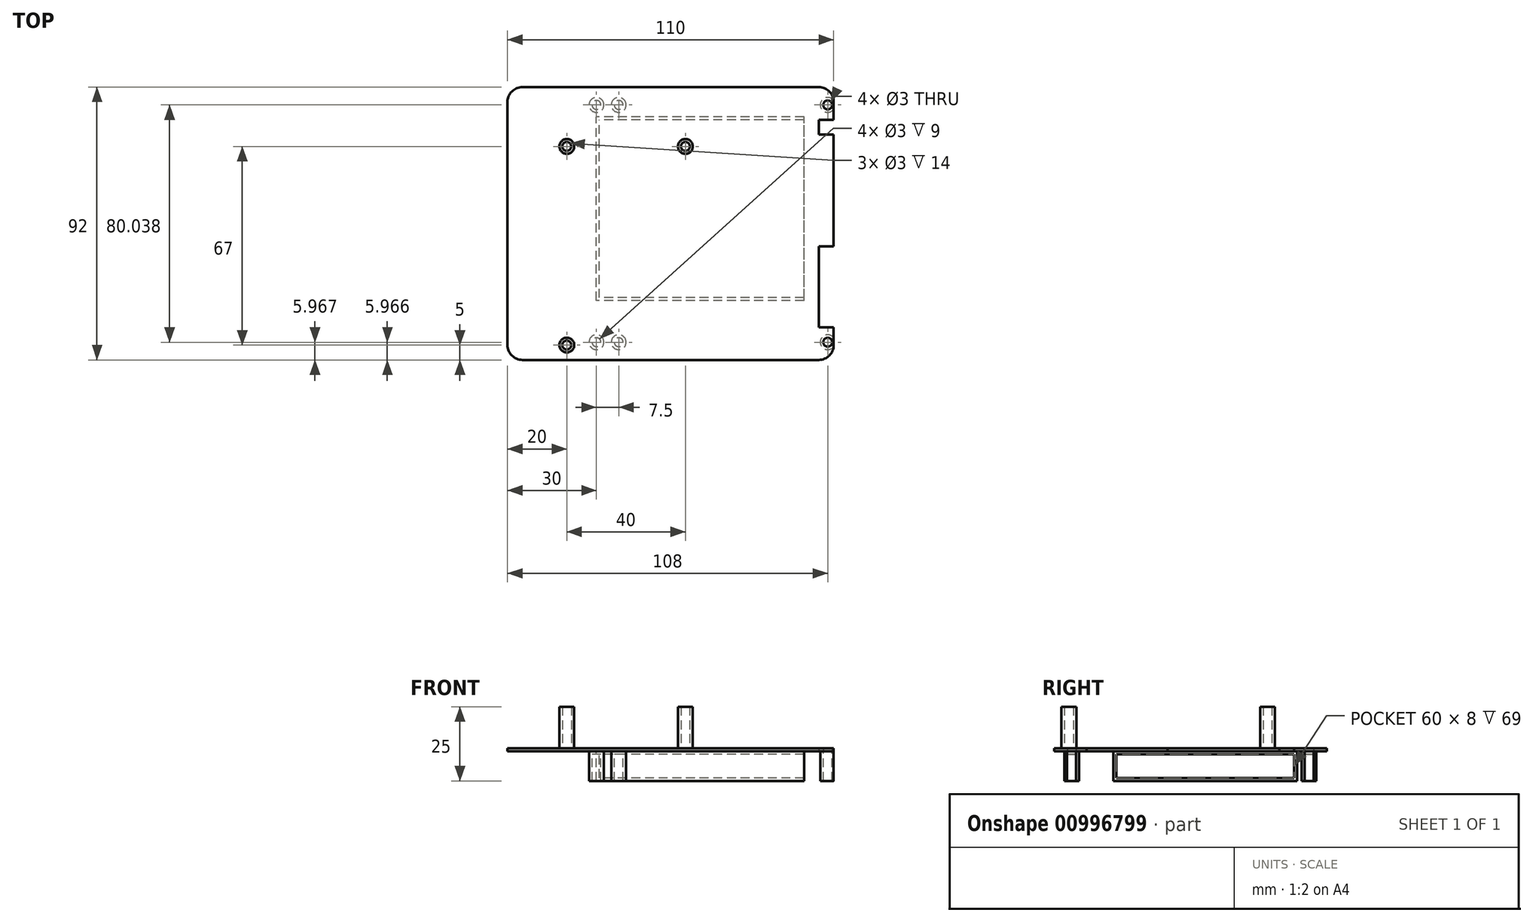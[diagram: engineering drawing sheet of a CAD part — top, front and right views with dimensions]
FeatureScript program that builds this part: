
annotation { "Feature Type Name" : "Feature", "Feature Type Description" : "" }
export const myFeature = defineFeature(function(context is Context, id is Id, definition is map)
    precondition{}
    {
        {
            var Q0;
            Q0=qCreatedBy(makeId("Top.planeOp"),FACE);
            var sketch = newSketch(context, id + "F0", { "sketchPlane" : qUnion([Q0])});
            skLineSegment(sketch, "E0.bottom", {"start": v(-50, -46) * mm, "end": v(50, -46) * mm});
            skLineSegment(sketch, "E0.top", {"start": v(-50, 46) * mm, "end": v(50, 46) * mm});
            skLineSegment(sketch, "E0.left", {"start": v(-55, -41) * mm, "end": v(-55, 41) * mm});
            skLineSegment(sketch, "E0.right", {"start": v(55, -41) * mm, "end": v(55, -35.05) * mm});
            skPoint(sketch, "E0.middle", {"position": v(0, 0) * mm});
            skPoint(sketch, "E1.visualSharp", {"position": v(-55, 46) * mm});
            skArc(sketch, "E1.filletArc", {"start": v(-50, 46) * mm, "mid": v(-53.54, 44.54) * mm, "end": v(-55, 41) * mm});
            skPoint(sketch, "E2.visualSharp", {"position": v(55, 46) * mm});
            skArc(sketch, "E2.filletArc", {"start": v(55, 41) * mm, "mid": v(53.54, 44.54) * mm, "end": v(50, 46) * mm});
            skPoint(sketch, "E3.visualSharp", {"position": v(55, -46) * mm});
            skArc(sketch, "E3.filletArc", {"start": v(50, -46) * mm, "mid": v(53.54, -44.54) * mm, "end": v(55, -41) * mm});
            skPoint(sketch, "E4.visualSharp", {"position": v(-55, -46) * mm});
            skArc(sketch, "E4.filletArc", {"start": v(-55, -41) * mm, "mid": v(-53.54, -44.54) * mm, "end": v(-50, -46) * mm});
            skCircle(sketch, "E5", {"center": v(-35, 26) * mm, "radius": 2.5 * mm});
            skCircle(sketch, "E6", {"center": v(-35, 26) * mm, "radius": 1.5 * mm});
            skCircle(sketch, "E7", {"center": v(5, 26) * mm, "radius": 1.5 * mm});
            skCircle(sketch, "E8", {"center": v(5, 26) * mm, "radius": 2.5 * mm});
            skCircle(sketch, "E9", {"center": v(53, 40) * mm, "radius": 1.5 * mm});
            skCircle(sketch, "E10", {"center": v(53, -40.03) * mm, "radius": 1.5 * mm});
            skCircle(sketch, "E11", {"center": v(-35, -41) * mm, "radius": 1.5 * mm});
            skCircle(sketch, "E12", {"center": v(-35, -41) * mm, "radius": 2.5 * mm});
            skLineSegment(sketch, "E13", {"start": v(50, -35.05) * mm, "end": v(50, -7.65) * mm});
            skLineSegment(sketch, "E14", {"start": v(50, -7.65) * mm, "end": v(55, -7.65) * mm});
            skLineSegment(sketch, "E15", {"start": v(55, -7.65) * mm, "end": v(55, -7.65) * mm});
            skLineSegment(sketch, "E16", {"start": v(50, -35.05) * mm, "end": v(55, -35.05) * mm});
            skPoint(sketch, "E17.end.orphan", {"position": v(-50, -35.04) * mm});
            skPoint(sketch, "E17.start.orphan", {"position": v(-50, -7.64) * mm});
            skLineSegment(sketch, "E18.trimOffspring", {"start": v(55, -7.65) * mm, "end": v(55, 30) * mm});
            skLineSegment(sketch, "E19", {"start": v(55, 35) * mm, "end": v(50, 35) * mm});
            skLineSegment(sketch, "E20", {"start": v(50, 35) * mm, "end": v(50, 30) * mm});
            skLineSegment(sketch, "E21", {"start": v(50, 30) * mm, "end": v(55, 30) * mm});
            skPoint(sketch, "E21.endSnap0", {"position": v(55, 16.67) * mm});
            skLineSegment(sketch, "E22.trimOffspring", {"start": v(55, 35) * mm, "end": v(55, 41) * mm});
            skArc(sketch, "E23", {"start": v(54.97, 41.54) * mm, "mid": v(50.5, 39.98) * mm, "end": v(55, 38.5) * mm});
            skArc(sketch, "E24", {"start": v(55, -38.53) * mm, "mid": v(50.5, -40) * mm, "end": v(54.97, -41.58) * mm});
            skSolve(sketch);
        }
        {
            var Q0;
            Q0=makeQuery(id+"F0.imprint","IMPRINT",FACE,{"disambiguationData":[TD([[makeQuery(id+"F0.imprint","IMPRINT",EDGE,{"derivedFrom":sQuery(id+"F0.wireOp",EDGE,"E0.bottom")}),1.0]])]});
            var Q1;
            Q1=makeQuery(id+"F0.imprint","IMPRINT",FACE,{"disambiguationData":[TD([[makeQuery(id+"F0.imprint","IMPRINT",EDGE,{"derivedFrom":sQuery(id+"F0.wireOp",EDGE,"E7")}),1.0]])]});
            var Q2;
            Q2=makeQuery(id+"F0.imprint","IMPRINT",FACE,{"disambiguationData":[TD([[makeQuery(id+"F0.imprint","IMPRINT",EDGE,{"derivedFrom":sQuery(id+"F0.wireOp",EDGE,"E6")}),1.0]])]});
            var Q3;
            Q3=makeQuery(id+"F0.imprint","IMPRINT",FACE,{"disambiguationData":[TD([[makeQuery(id+"F0.imprint","IMPRINT",EDGE,{"derivedFrom":sQuery(id+"F0.wireOp",EDGE,"E11")}),-1.0]])]});
            var Q4;
            Q4=makeQuery(id+"F0.imprint","IMPRINT",FACE,{"disambiguationData":[TD([[makeQuery(id+"F0.imprint","IMPRINT",EDGE,{"derivedFrom":sQuery(id+"F0.wireOp",EDGE,"E11")}),1.0]])]});
            var Q5;
            Q5=makeQuery(id+"F0.imprint","IMPRINT",FACE,{"disambiguationData":[TD([[makeQuery(id+"F0.imprint","IMPRINT",EDGE,{"derivedFrom":sQuery(id+"F0.wireOp",EDGE,"E5")}),1.0]])]});
            var Q6;
            Q6=makeQuery(id+"F0.imprint","IMPRINT",FACE,{"disambiguationData":[TD([[makeQuery(id+"F0.imprint","IMPRINT",EDGE,{"derivedFrom":sQuery(id+"F0.wireOp",EDGE,"E7")}),-1.0]])]});
            var Q7;
            Q7=makeQuery(id+"F0.imprint","IMPRINT",FACE,{"disambiguationData":[TD([[makeQuery(id+"F0.imprint","IMPRINT",EDGE,{"derivedFrom":sQuery(id+"F0.wireOp",EDGE,"E9")}),-1.0]])]});
            var Q8;
            Q8=makeQuery(id+"F0.imprint","IMPRINT",FACE,{"disambiguationData":[TD([[makeQuery(id+"F0.imprint","IMPRINT",EDGE,{"derivedFrom":sQuery(id+"F0.wireOp",EDGE,"E10")}),-1.0]])]});
            extrude(context, id + "F1", {"entities" : qUnion([Q0, Q1, Q2, Q3, Q4, Q5, Q6, Q7, Q8]), "depth" : 1 * mm, "offsetDistance" : 25 * mm});
        }
        {
            var Q0;
            Q0=makeQuery(id+"F0.imprint","IMPRINT",FACE,{"disambiguationData":[TD([[makeQuery(id+"F0.imprint","IMPRINT",EDGE,{"derivedFrom":sQuery(id+"F0.wireOp",EDGE,"E5")}),1.0]])]});
            var Q1;
            Q1=makeQuery(id+"F0.imprint","IMPRINT",FACE,{"disambiguationData":[TD([[makeQuery(id+"F0.imprint","IMPRINT",EDGE,{"derivedFrom":sQuery(id+"F0.wireOp",EDGE,"E7")}),-1.0]])]});
            var Q2;
            Q2=makeQuery(id+"F0.imprint","IMPRINT",FACE,{"disambiguationData":[TD([[makeQuery(id+"F0.imprint","IMPRINT",EDGE,{"derivedFrom":sQuery(id+"F0.wireOp",EDGE,"E11")}),-1.0]])]});
            extrude(context, id + "F2", {"entities" : qUnion([Q0, Q1, Q2]), "operationType" : NewBodyOperationType.ADD, "depth" : 15 * mm, "offsetDistance" : 25 * mm});
        }
        {
            var Q0;
            Q0=qCreatedBy(makeId("Top.planeOp"),FACE);
            var sketch = newSketch(context, id + "F3", { "sketchPlane" : qUnion([Q0])});
            skPoint(sketch, "E25.middle", {"position": v(10, 5) * mm});
            skLineSegment(sketch, "E26.bottom", {"start": v(45, -26) * mm, "end": v(-25, -26) * mm});
            skLineSegment(sketch, "E26.top", {"start": v(45, 36) * mm, "end": v(-25, 36) * mm});
            skLineSegment(sketch, "E26.left", {"start": v(45, -26) * mm, "end": v(45, 36) * mm});
            skLineSegment(sketch, "E26.right", {"start": v(-25, -26) * mm, "end": v(-25, 36) * mm});
            skPoint(sketch, "E25.bottom.end.orphan", {"position": v(-24, -25) * mm});
            skPoint(sketch, "E25.top.end.orphan", {"position": v(-24, 35) * mm});
            skPoint(sketch, "E25.left.end.orphan", {"position": v(44, 35) * mm});
            skPoint(sketch, "E25.left.start.orphan", {"position": v(44, -25) * mm});
            skCircle(sketch, "E27", {"center": v(-17.5, -40.03) * mm, "radius": 2.5 * mm});
            skCircle(sketch, "E28", {"center": v(-17.5, 40) * mm, "radius": 2.5 * mm});
            skCircle(sketch, "E29", {"center": v(-25, -40.03) * mm, "radius": 2.5 * mm});
            skCircle(sketch, "E30", {"center": v(-25, 40) * mm, "radius": 2.5 * mm});
            skSolve(sketch);
        }
        {
            var Q0;
            Q0=makeQuery(id+"F3.imprint","IMPRINT",FACE,{"disambiguationData":[TD([[makeQuery(id+"F3.imprint","IMPRINT",EDGE,{"derivedFrom":sQuery(id+"F3.wireOp",EDGE,"E26.bottom")}),-1.0]])]});
            var Q1;
            Q1=makeQuery(id+"F3.imprint","IMPRINT",FACE,{"disambiguationData":[TD([[makeQuery(id+"F3.imprint","IMPRINT",EDGE,{"derivedFrom":sQuery(id+"F3.wireOp",EDGE,"E27")}),1.0]])]});
            var Q2;
            Q2=makeQuery(id+"F3.imprint","IMPRINT",FACE,{"disambiguationData":[TD([[makeQuery(id+"F3.imprint","IMPRINT",EDGE,{"derivedFrom":sQuery(id+"F3.wireOp",EDGE,"E28")}),1.0]])]});
            var Q3;
            Q3=makeQuery(id+"F3.imprint","IMPRINT",FACE,{"disambiguationData":[TD([[makeQuery(id+"F3.imprint","IMPRINT",EDGE,{"derivedFrom":sQuery(id+"F3.wireOp",EDGE,"E29")}),1.0]])]});
            var Q4;
            Q4=makeQuery(id+"F3.imprint","IMPRINT",FACE,{"disambiguationData":[TD([[makeQuery(id+"F3.imprint","IMPRINT",EDGE,{"derivedFrom":sQuery(id+"F3.wireOp",EDGE,"E30")}),1.0]])]});
            var Q5;
            Q5=makeQuery(id+"F0.imprint","IMPRINT",FACE,{"disambiguationData":[TD([[makeQuery(id+"F0.imprint","IMPRINT",EDGE,{"derivedFrom":sQuery(id+"F0.wireOp",EDGE,"E9")}),-1.0]])]});
            var Q6;
            Q6=makeQuery(id+"F0.imprint","IMPRINT",FACE,{"disambiguationData":[TD([[makeQuery(id+"F0.imprint","IMPRINT",EDGE,{"derivedFrom":sQuery(id+"F0.wireOp",EDGE,"E10")}),-1.0]])]});
            extrude(context, id + "F4", {"entities" : qUnion([Q0, Q1, Q2, Q3, Q4, Q5, Q6]), "oppositeDirection" : true, "depth" : 10 * mm, "offsetDistance" : 25 * mm});
        }
        {
            var Q0;
            Q0=makeQuery(id+"F4.opExtrude","SWEPT_FACE",FACE,{"disambiguationData":[OSD([sQuery(id+"F3.wireOp",EDGE,"E26.left")])]});
            var Q1;
            Q1=makeQuery(id+"F4.opExtrude","CAP_FACE",FACE,{"disambiguationData":[OSD([sQuery(id+"F3.wireOp",EDGE,"E27")])],"isStart":false});
            var Q2;
            Q2=makeQuery(id+"F4.opExtrude","CAP_FACE",FACE,{"disambiguationData":[OSD([sQuery(id+"F3.wireOp",EDGE,"E28")])],"isStart":false});
            var Q3;
            Q3=makeQuery(id+"F4.opExtrude","CAP_FACE",FACE,{"disambiguationData":[OSD([sQuery(id+"F3.wireOp",EDGE,"E29")])],"isStart":false});
            var Q4;
            Q4=makeQuery(id+"F4.opExtrude","CAP_FACE",FACE,{"disambiguationData":[OSD([sQuery(id+"F3.wireOp",EDGE,"E30")])],"isStart":false});
            shell(context, id + "F5", {"entities" : qUnion([Q0, Q1, Q2, Q3, Q4]), "thickness" : 1 * mm});
        }
    });
